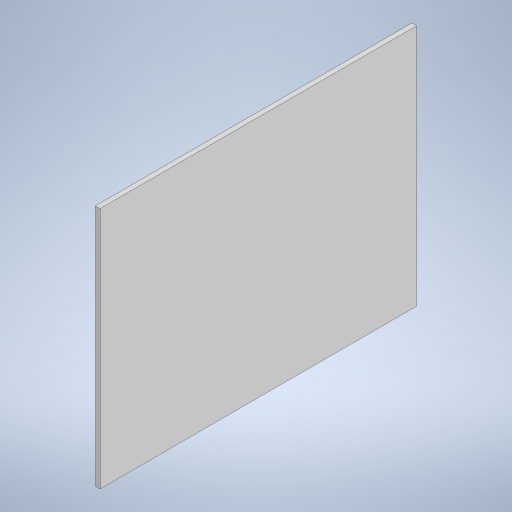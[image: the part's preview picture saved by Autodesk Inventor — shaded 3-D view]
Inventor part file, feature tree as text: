
AUTODESK INVENTOR PART (.ipt)
format: ipt  version: 2024.3 (Build 283343000, 343)  size: 187,392 bytes
history: native  units: mm
features: extrude x1, sketch x1
ambient origin geometry x8: Origin, YZ Plane, XZ Plane, XY Plane, X Axis, Y Axis, Z Axis, Center Point
bodies: Solid1 (feature_tree)
feature tree (2):
  extrude  "Extrusion1"  Depth=153.427mm
  sketch  "Sketch1"  dims[d0=200.0mm d1=153.427mm d2=3.0mm d3=0.0mm]
